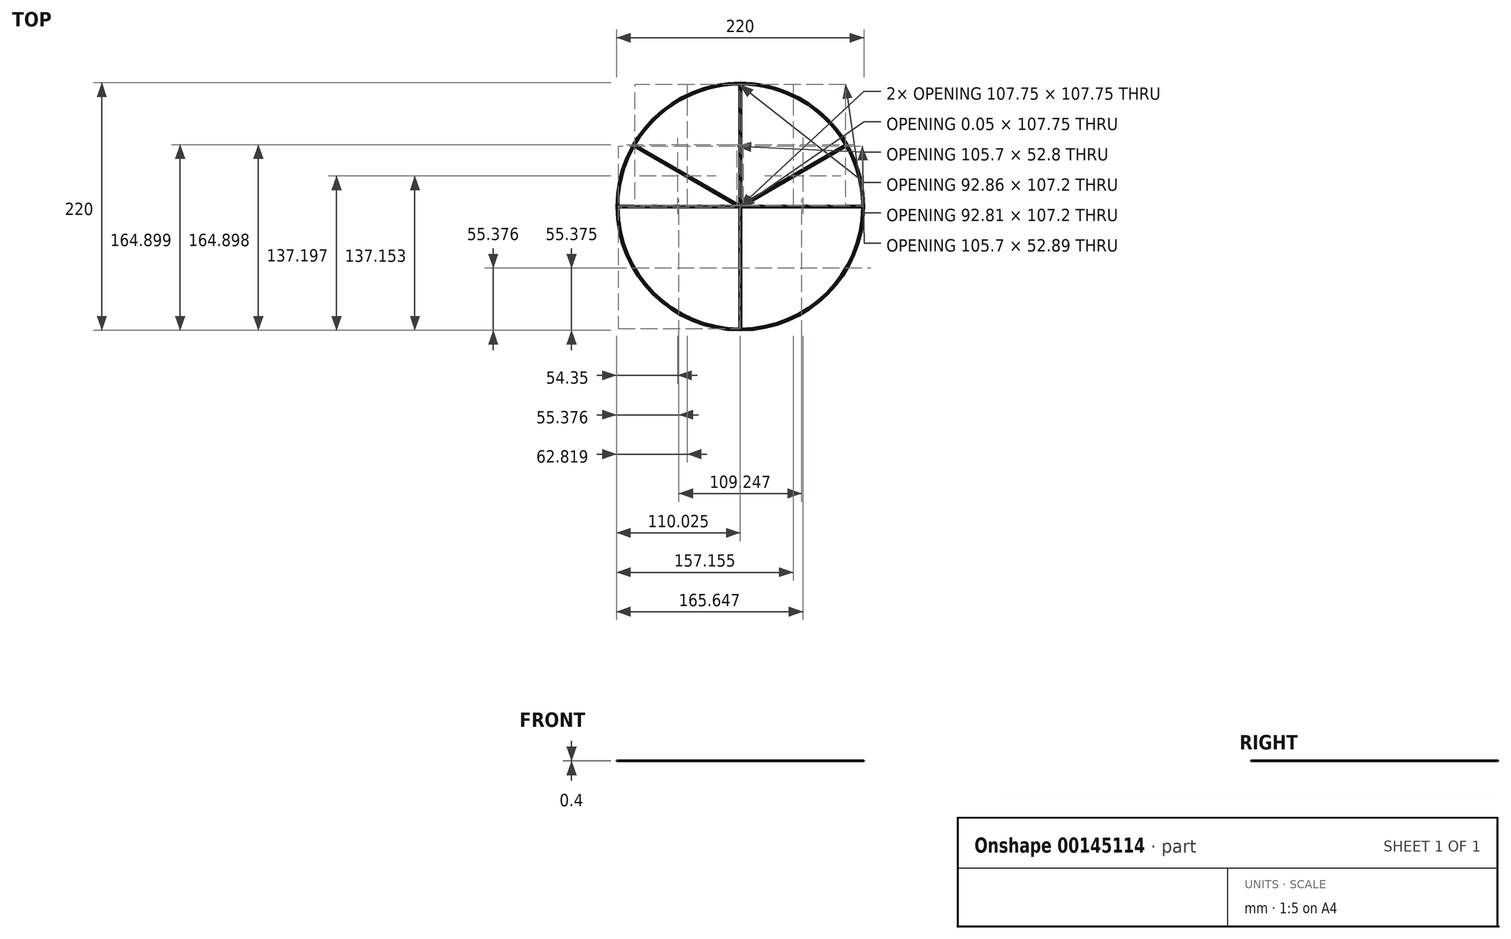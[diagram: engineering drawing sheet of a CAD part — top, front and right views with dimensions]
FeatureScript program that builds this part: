
annotation { "Feature Type Name" : "Feature", "Feature Type Description" : "" }
export const myFeature = defineFeature(function(context is Context, id is Id, definition is map)
    precondition{}
    {
        {
            var Q0;
            Q0=qCreatedBy(makeId("Top.planeOp"),FACE);
            var sketch = newSketch(context, id + "F0", { "sketchPlane" : qUnion([Q0])});
            skCircle(sketch, "E0", {"center": v(0, 0) * mm, "radius": 110 * mm});
            skCircle(sketch, "E1", {"center": v(0, 0) * mm, "radius": 108.5 * mm});
            skLineSegment(sketch, "E2", {"start": v(0, 108.5) * mm, "end": v(0, -108.5) * mm});
            skLineSegment(sketch, "E3", {"start": v(-108.5, 0) * mm, "end": v(108.5, 0) * mm});
            skLineSegment(sketch, "E4", {"start": v(0, 0) * mm, "end": v(93.94, 54.3) * mm});
            skLineSegment(sketch, "E5", {"start": v(0, 0) * mm, "end": v(0.05, -108.5) * mm});
            skLineSegment(sketch, "E6", {"start": v(0, 0) * mm, "end": v(-93.99, 54.2) * mm});
            skLineSegment(sketch, "E7.0", {"start": v(0.38, -0.65) * mm, "end": v(94.31, 53.64) * mm});
            skLineSegment(sketch, "E8.0", {"start": v(-0.38, 0.65) * mm, "end": v(93.56, 54.94) * mm});
            skLineSegment(sketch, "E9.0", {"start": v(-0.38, -0.65) * mm, "end": v(-94.36, 53.55) * mm});
            skLineSegment(sketch, "E10.0", {"start": v(0.38, 0.65) * mm, "end": v(-93.61, 54.85) * mm});
            skPoint(sketch, "E11", {"position": v(-5.02, 2.03) * mm});
            skPoint(sketch, "E12", {"position": v(5.01, 2.03) * mm});
            skPoint(sketch, "E13", {"position": v(0, 0.87) * mm});
            skLineSegment(sketch, "E14.0", {"start": v(-108.5, -0.75) * mm, "end": v(108.5, -0.75) * mm});
            skLineSegment(sketch, "E15.0", {"start": v(-108.5, 0.75) * mm, "end": v(108.5, 0.75) * mm});
            skLineSegment(sketch, "E16.0", {"start": v(-0.75, 108.5) * mm, "end": v(-0.75, -108.5) * mm});
            skLineSegment(sketch, "E17.0", {"start": v(0.75, 108.5) * mm, "end": v(0.75, -108.5) * mm});
            skSolve(sketch);
        }
        {
            var Q0;
            Q0=makeQuery(id+"F0.imprint","IMPRINT",FACE,{"disambiguationData":[TD([[makeQuery(id+"F0.imprint","IMPRINT",EDGE,{"derivedFrom":sQuery(id+"F0.wireOp",EDGE,"E0")}),1.0]])]});
            var Q1;
            {var subQ0=sQuery(id+"F0.wireOp",EDGE,"E6");Q1=makeQuery(id+"F0.imprint","IMPRINT",FACE,{"disambiguationData":[TD([[makeQuery(id+"F0.imprint","IMPRINT",EDGE,{"derivedFrom":subQ0}),1.0]])]});}
            var Q2;
            {var subQ0=sQuery(id+"F0.wireOp",EDGE,"E6");Q2=makeQuery(id+"F0.imprint","IMPRINT",FACE,{"disambiguationData":[TD([[makeQuery(id+"F0.imprint","IMPRINT",EDGE,{"derivedFrom":subQ0}),-1.0]])]});}
            var Q3;
            {var subQ0=sQuery(id+"F0.wireOp",EDGE,"E5");Q3=makeQuery(id+"F0.imprint","IMPRINT",FACE,{"disambiguationData":[TD([[makeQuery(id+"F0.imprint","IMPRINT",EDGE,{"derivedFrom":subQ0}),-1.0]])]});}
            var Q4;
            {var subQ0=sQuery(id+"F0.wireOp",EDGE,"E5");Q4=makeQuery(id+"F0.imprint","IMPRINT",FACE,{"disambiguationData":[TD([[makeQuery(id+"F0.imprint","IMPRINT",EDGE,{"derivedFrom":subQ0}),1.0]])]});}
            var Q5;
            {var subQ0=sQuery(id+"F0.wireOp",EDGE,"E4");Q5=makeQuery(id+"F0.imprint","IMPRINT",FACE,{"disambiguationData":[TD([[makeQuery(id+"F0.imprint","IMPRINT",EDGE,{"derivedFrom":subQ0}),-1.0]])]});}
            var Q6;
            {var subQ0=sQuery(id+"F0.wireOp",EDGE,"E4");Q6=makeQuery(id+"F0.imprint","IMPRINT",FACE,{"disambiguationData":[TD([[makeQuery(id+"F0.imprint","IMPRINT",EDGE,{"derivedFrom":subQ0}),1.0]])]});}
            var Q7;
            {var subQ0=sQuery(id+"F0.wireOp",EDGE,"9c54c420-31e8-4f59-a4ee-cd0e4fd99867.0");var subQ1=sQuery(id+"F0.wireOp",EDGE,"E3");var subQ2=makeQuery(id+"F0.imprint","INTERSECT",VERTEX,{"derivedFrom":[subQ1,subQ0]});Q7=makeQuery(id+"F0.imprint","IMPRINT",FACE,{"disambiguationData":[TD([[makeQuery(id+"F0.imprint","IMPRINT",EDGE,{"disambiguationData":[TD([[subQ2,-1.0]])],"derivedFrom":subQ1}),-1.0]])]});}
            var Q8;
            {var subQ0=sQuery(id+"F0.wireOp",EDGE,"e9ea2af9-b296-4bc3-a3ab-09d7b7e77eb5.0");var subQ1=sQuery(id+"F0.wireOp",EDGE,"E3");var subQ2=makeQuery(id+"F0.imprint","INTERSECT",VERTEX,{"derivedFrom":[subQ1,subQ0]});Q8=makeQuery(id+"F0.imprint","IMPRINT",FACE,{"disambiguationData":[TD([[makeQuery(id+"F0.imprint","IMPRINT",EDGE,{"disambiguationData":[TD([[subQ2,1.0]])],"derivedFrom":subQ1}),-1.0]])]});}
            var Q9;
            {var subQ1=sQuery(id+"F0.wireOp",EDGE,"E1");var subQ7=sQuery(id+"F0.wireOp",EDGE,"E3");var subQ9=makeQuery(id+"F0.imprint","INTERSECT",VERTEX,{"disambiguationData":[OD(0.0)],"derivedFrom":[subQ1,subQ7]});Q9=makeQuery(id+"F0.imprint","IMPRINT",FACE,{"disambiguationData":[TD([[makeQuery(id+"F0.imprint","IMPRINT",EDGE,{"disambiguationData":[TD([[subQ9,-1.0]])],"derivedFrom":subQ1}),1.0]])]});}
            var Q10;
            {var subQ0=sQuery(id+"F0.wireOp",EDGE,"E3");var subQ1=sQuery(id+"F0.wireOp",EDGE,"E1");var subQ2=makeQuery(id+"F0.imprint","INTERSECT",VERTEX,{"disambiguationData":[OD(0.0)],"derivedFrom":[subQ1,subQ0]});Q10=makeQuery(id+"F0.imprint","IMPRINT",FACE,{"disambiguationData":[TD([[makeQuery(id+"F0.imprint","IMPRINT",EDGE,{"disambiguationData":[TD([[subQ2,1.0]])],"derivedFrom":subQ1}),1.0]])]});}
            var Q11;
            {var subQ0=sQuery(id+"F0.wireOp",EDGE,"E6");var subQ1=sQuery(id+"F0.wireOp",EDGE,"E1");var subQ2=makeQuery(id+"F0.imprint","INTERSECT",VERTEX,{"derivedFrom":[subQ1,subQ0]});Q11=makeQuery(id+"F0.imprint","IMPRINT",FACE,{"disambiguationData":[TD([[makeQuery(id+"F0.imprint","IMPRINT",EDGE,{"disambiguationData":[TD([[subQ2,-1.0]])],"derivedFrom":subQ1}),1.0]])]});}
            var Q12;
            {var subQ1=sQuery(id+"F0.wireOp",EDGE,"E6");var subQ6=sQuery(id+"F0.wireOp",EDGE,"E1");var subQ9=makeQuery(id+"F0.imprint","INTERSECT",VERTEX,{"derivedFrom":[subQ6,subQ1]});Q12=makeQuery(id+"F0.imprint","IMPRINT",FACE,{"disambiguationData":[TD([[makeQuery(id+"F0.imprint","IMPRINT",EDGE,{"disambiguationData":[TD([[subQ9,1.0]])],"derivedFrom":subQ6}),1.0]])]});}
            var Q13;
            {var subQ1=sQuery(id+"F0.wireOp",EDGE,"E2");var subQ6=sQuery(id+"F0.wireOp",EDGE,"E1");var subQ9=makeQuery(id+"F0.imprint","INTERSECT",VERTEX,{"disambiguationData":[OD(0.0)],"derivedFrom":[subQ6,subQ1]});Q13=makeQuery(id+"F0.imprint","IMPRINT",FACE,{"disambiguationData":[TD([[makeQuery(id+"F0.imprint","IMPRINT",EDGE,{"disambiguationData":[TD([[subQ9,-1.0]])],"derivedFrom":subQ6}),1.0]])]});}
            var Q14;
            {var subQ0=sQuery(id+"F0.wireOp",EDGE,"E2");var subQ1=sQuery(id+"F0.wireOp",EDGE,"E1");var subQ2=makeQuery(id+"F0.imprint","INTERSECT",VERTEX,{"disambiguationData":[OD(0.0)],"derivedFrom":[subQ1,subQ0]});Q14=makeQuery(id+"F0.imprint","IMPRINT",FACE,{"disambiguationData":[TD([[makeQuery(id+"F0.imprint","IMPRINT",EDGE,{"disambiguationData":[TD([[subQ2,1.0]])],"derivedFrom":subQ1}),1.0]])]});}
            var Q15;
            {var subQ1=sQuery(id+"F0.wireOp",EDGE,"E1");var subQ7=sQuery(id+"F0.wireOp",EDGE,"E4");var subQ9=makeQuery(id+"F0.imprint","INTERSECT",VERTEX,{"derivedFrom":[subQ1,subQ7]});Q15=makeQuery(id+"F0.imprint","IMPRINT",FACE,{"disambiguationData":[TD([[makeQuery(id+"F0.imprint","IMPRINT",EDGE,{"disambiguationData":[TD([[subQ9,-1.0]])],"derivedFrom":subQ1}),1.0]])]});}
            var Q16;
            {var subQ0=sQuery(id+"F0.wireOp",EDGE,"E4");var subQ1=sQuery(id+"F0.wireOp",EDGE,"E1");var subQ2=makeQuery(id+"F0.imprint","INTERSECT",VERTEX,{"derivedFrom":[subQ1,subQ0]});Q16=makeQuery(id+"F0.imprint","IMPRINT",FACE,{"disambiguationData":[TD([[makeQuery(id+"F0.imprint","IMPRINT",EDGE,{"disambiguationData":[TD([[subQ2,1.0]])],"derivedFrom":subQ1}),1.0]])]});}
            var Q17;
            {var subQ0=sQuery(id+"F0.wireOp",EDGE,"E3");var subQ1=sQuery(id+"F0.wireOp",EDGE,"E1");var subQ2=makeQuery(id+"F0.imprint","INTERSECT",VERTEX,{"disambiguationData":[OD(1.0)],"derivedFrom":[subQ1,subQ0]});Q17=makeQuery(id+"F0.imprint","IMPRINT",FACE,{"disambiguationData":[TD([[makeQuery(id+"F0.imprint","IMPRINT",EDGE,{"disambiguationData":[TD([[subQ2,-1.0]])],"derivedFrom":subQ1}),1.0]])]});}
            var Q18;
            {var subQ1=sQuery(id+"F0.wireOp",EDGE,"E1");var subQ7=sQuery(id+"F0.wireOp",EDGE,"E3");var subQ9=makeQuery(id+"F0.imprint","INTERSECT",VERTEX,{"disambiguationData":[OD(1.0)],"derivedFrom":[subQ1,subQ7]});Q18=makeQuery(id+"F0.imprint","IMPRINT",FACE,{"disambiguationData":[TD([[makeQuery(id+"F0.imprint","IMPRINT",EDGE,{"disambiguationData":[TD([[subQ9,1.0]])],"derivedFrom":subQ1}),1.0]])]});}
            var Q19;
            {var subQ0=sQuery(id+"F0.wireOp",EDGE,"E2");var subQ1=sQuery(id+"F0.wireOp",EDGE,"E1");var subQ2=makeQuery(id+"F0.imprint","INTERSECT",VERTEX,{"disambiguationData":[OD(1.0)],"derivedFrom":[subQ1,subQ0]});Q19=makeQuery(id+"F0.imprint","IMPRINT",FACE,{"disambiguationData":[TD([[makeQuery(id+"F0.imprint","IMPRINT",EDGE,{"disambiguationData":[TD([[subQ2,1.0]])],"derivedFrom":subQ1}),1.0]])]});}
            var Q20;
            {var subQ0=sQuery(id+"F0.wireOp",EDGE,"E9.0");var subQ1=sQuery(id+"F0.wireOp",EDGE,"E3");var subQ2=makeQuery(id+"F0.imprint","INTERSECT",VERTEX,{"derivedFrom":[subQ1,subQ0]});Q20=makeQuery(id+"F0.imprint","IMPRINT",FACE,{"disambiguationData":[TD([[makeQuery(id+"F0.imprint","IMPRINT",EDGE,{"disambiguationData":[TD([[subQ2,-1.0]])],"derivedFrom":subQ1}),1.0]])]});}
            var Q21;
            {var subQ5=sQuery(id+"F0.wireOp",EDGE,"E3");var subQ7=sQuery(id+"F0.wireOp",EDGE,"E17.0");var subQ8=makeQuery(id+"F0.imprint","INTERSECT",VERTEX,{"derivedFrom":[subQ5,subQ7]});Q21=makeQuery(id+"F0.imprint","IMPRINT",FACE,{"disambiguationData":[TD([[makeQuery(id+"F0.imprint","IMPRINT",EDGE,{"disambiguationData":[TD([[subQ8,-1.0]])],"derivedFrom":subQ5}),1.0]])]});}
            var Q22;
            {var subQ0=sQuery(id+"F0.wireOp",EDGE,"E15.0");var subQ1=makeQuery(id+"F0.imprint","INTERSECT",VERTEX,{"derivedFrom":[sQuery(id+"F0.wireOp",EDGE,"E10.0"),subQ0]});Q22=makeQuery(id+"F0.imprint","IMPRINT",FACE,{"disambiguationData":[TD([[makeQuery(id+"F0.imprint","IMPRINT",EDGE,{"disambiguationData":[TD([[subQ1,1.0]])],"derivedFrom":subQ0}),-1.0]])]});}
            var Q23;
            {var subQ0=sQuery(id+"F0.wireOp",EDGE,"E15.0");var subQ1=makeQuery(id+"F0.imprint","INTERSECT",VERTEX,{"derivedFrom":[sQuery(id+"F0.wireOp",EDGE,"E8.0"),subQ0]});Q23=makeQuery(id+"F0.imprint","IMPRINT",FACE,{"disambiguationData":[TD([[makeQuery(id+"F0.imprint","IMPRINT",EDGE,{"disambiguationData":[TD([[subQ1,1.0]])],"derivedFrom":subQ0}),-1.0]])]});}
            var Q24;
            {var subQ0=sQuery(id+"F0.wireOp",EDGE,"E15.0");var subQ1=sQuery(id+"F0.wireOp",EDGE,"E8.0");var subQ2=makeQuery(id+"F0.imprint","INTERSECT",VERTEX,{"derivedFrom":[subQ1,subQ0]});Q24=makeQuery(id+"F0.imprint","IMPRINT",FACE,{"disambiguationData":[TD([[makeQuery(id+"F0.imprint","IMPRINT",EDGE,{"disambiguationData":[TD([[subQ2,-1.0]])],"derivedFrom":subQ1}),1.0]])]});}
            var Q25;
            {var subQ0=sQuery(id+"F0.wireOp",EDGE,"E8.0");var subQ1=sQuery(id+"F0.wireOp",EDGE,"E2");var subQ2=makeQuery(id+"F0.imprint","INTERSECT",VERTEX,{"derivedFrom":[subQ1,subQ0]});Q25=makeQuery(id+"F0.imprint","IMPRINT",FACE,{"disambiguationData":[TD([[makeQuery(id+"F0.imprint","IMPRINT",EDGE,{"disambiguationData":[TD([[subQ2,-1.0]])],"derivedFrom":subQ1}),1.0]])]});}
            var Q26;
            {var subQ0=sQuery(id+"F0.wireOp",EDGE,"E10.0");var subQ1=sQuery(id+"F0.wireOp",EDGE,"E2");var subQ2=makeQuery(id+"F0.imprint","INTERSECT",VERTEX,{"derivedFrom":[subQ1,subQ0]});Q26=makeQuery(id+"F0.imprint","IMPRINT",FACE,{"disambiguationData":[TD([[makeQuery(id+"F0.imprint","IMPRINT",EDGE,{"disambiguationData":[TD([[subQ2,-1.0]])],"derivedFrom":subQ1}),1.0]])]});}
            var Q27;
            {var subQ0=sQuery(id+"F0.wireOp",EDGE,"E10.0");var subQ1=sQuery(id+"F0.wireOp",EDGE,"E2");var subQ2=makeQuery(id+"F0.imprint","INTERSECT",VERTEX,{"derivedFrom":[subQ1,subQ0]});Q27=makeQuery(id+"F0.imprint","IMPRINT",FACE,{"disambiguationData":[TD([[makeQuery(id+"F0.imprint","IMPRINT",EDGE,{"disambiguationData":[TD([[subQ2,-1.0]])],"derivedFrom":subQ1}),-1.0]])]});}
            var Q28;
            {var subQ0=sQuery(id+"F0.wireOp",EDGE,"E14.0");var subQ1=sQuery(id+"F0.wireOp",EDGE,"E2");var subQ2=makeQuery(id+"F0.imprint","INTERSECT",VERTEX,{"derivedFrom":[subQ1,subQ0]});Q28=makeQuery(id+"F0.imprint","IMPRINT",FACE,{"disambiguationData":[TD([[makeQuery(id+"F0.imprint","IMPRINT",EDGE,{"disambiguationData":[TD([[subQ2,1.0]])],"derivedFrom":subQ0}),1.0]])]});}
            var Q29;
            {var subQ4=sQuery(id+"F0.wireOp",EDGE,"E5");var subQ6=sQuery(id+"F0.wireOp",EDGE,"E14.0");var subQ7=makeQuery(id+"F0.imprint","INTERSECT",VERTEX,{"derivedFrom":[subQ4,subQ6]});Q29=makeQuery(id+"F0.imprint","IMPRINT",FACE,{"disambiguationData":[TD([[makeQuery(id+"F0.imprint","IMPRINT",EDGE,{"disambiguationData":[TD([[subQ7,-1.0]])],"derivedFrom":subQ6}),1.0]])]});}
            extrude(context, id + "F1", {"entities" : qUnion([Q0, Q1, Q2, Q3, Q4, Q5, Q6, Q7, Q8, Q9, Q10, Q11, Q12, Q13, Q14, Q15, Q16, Q17, Q18, Q19, Q20, Q21, Q22, Q23, Q24, Q25, Q26, Q27, Q28, Q29]), "depth" : .4 * mm});
        }
    });
